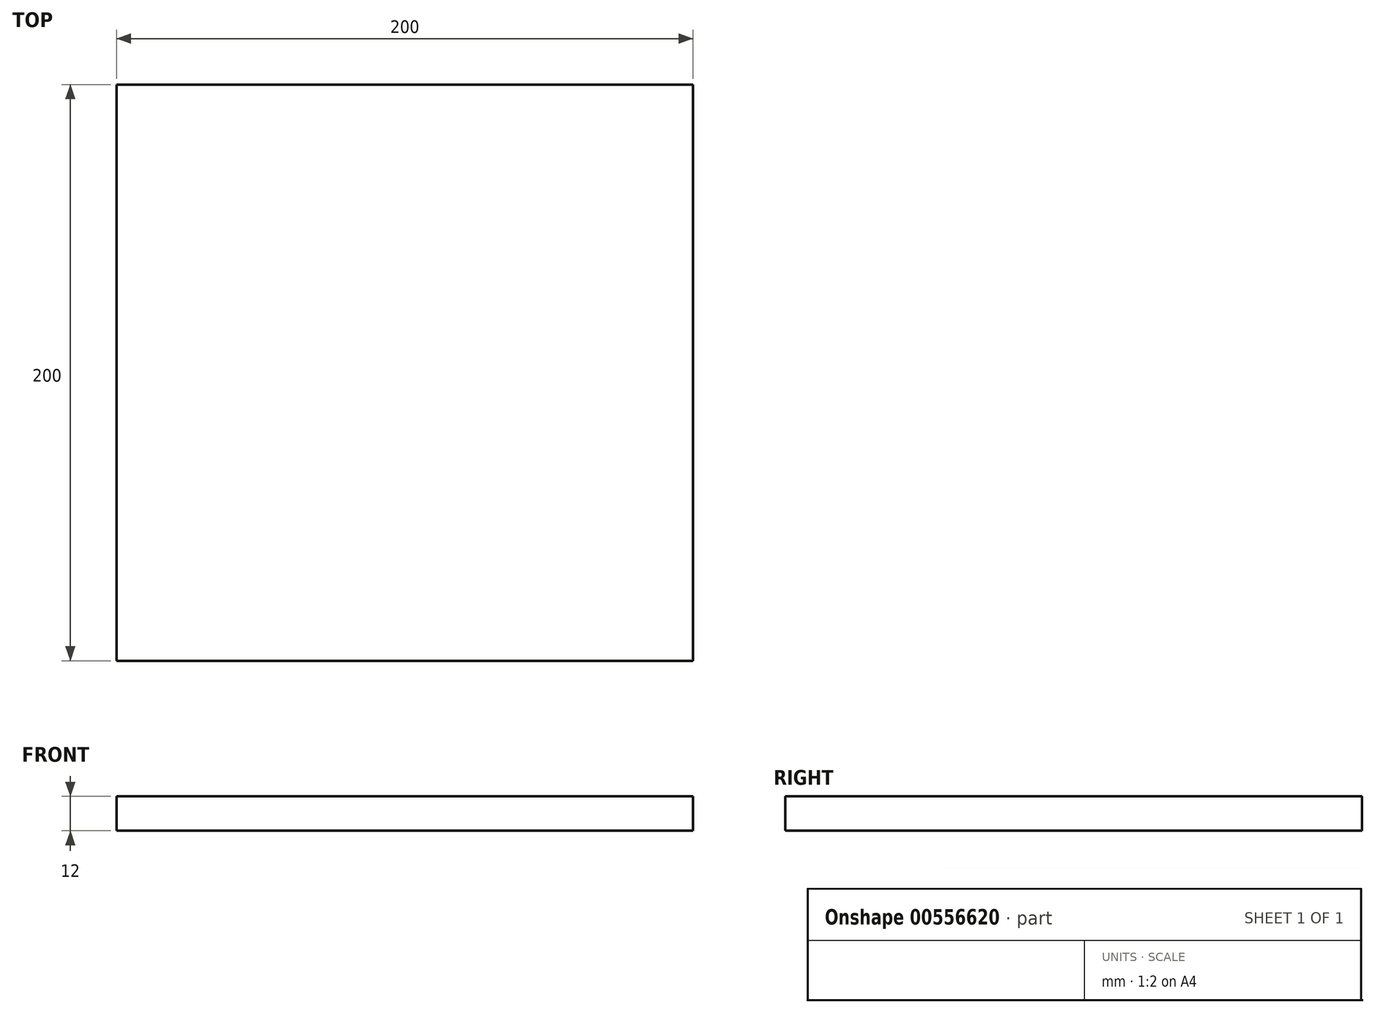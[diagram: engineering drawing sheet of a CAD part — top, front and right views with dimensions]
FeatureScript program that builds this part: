
annotation { "Feature Type Name" : "Feature", "Feature Type Description" : "" }
export const myFeature = defineFeature(function(context is Context, id is Id, definition is map)
    precondition{}
    {
        {
            var Q0;
            Q0=qCreatedBy(makeId("Top.planeOp"),FACE);
            var sketch = newSketch(context, id + "F0", { "sketchPlane" : qUnion([Q0])});
            skLineSegment(sketch, "E0", {"start": v(0, 0) * mm, "end": v(-200, 0) * mm});
            skLineSegment(sketch, "E1", {"start": v(-200, 0) * mm, "end": v(-200, 200) * mm});
            skLineSegment(sketch, "E2", {"start": v(-200, 200) * mm, "end": v(0, 200) * mm});
            skLineSegment(sketch, "E3", {"start": v(0, 200) * mm, "end": v(0, 0) * mm});
            skSolve(sketch);
        }
        {
            var Q0;
            Q0=makeQuery(id+"F0.imprint","IMPRINT",FACE,{"disambiguationData":[TD([[makeQuery(id+"F0.imprint","IMPRINT",EDGE,{"derivedFrom":sQuery(id+"F0.wireOp",EDGE,"E0")}),-1.0]])]});
            extrude(context, id + "F1", {"entities" : qUnion([Q0]), "endBound" : BoundingType.SYMMETRIC, "depth" : 12 * mm, "offsetDistance" : 25 * mm});
        }
    });
